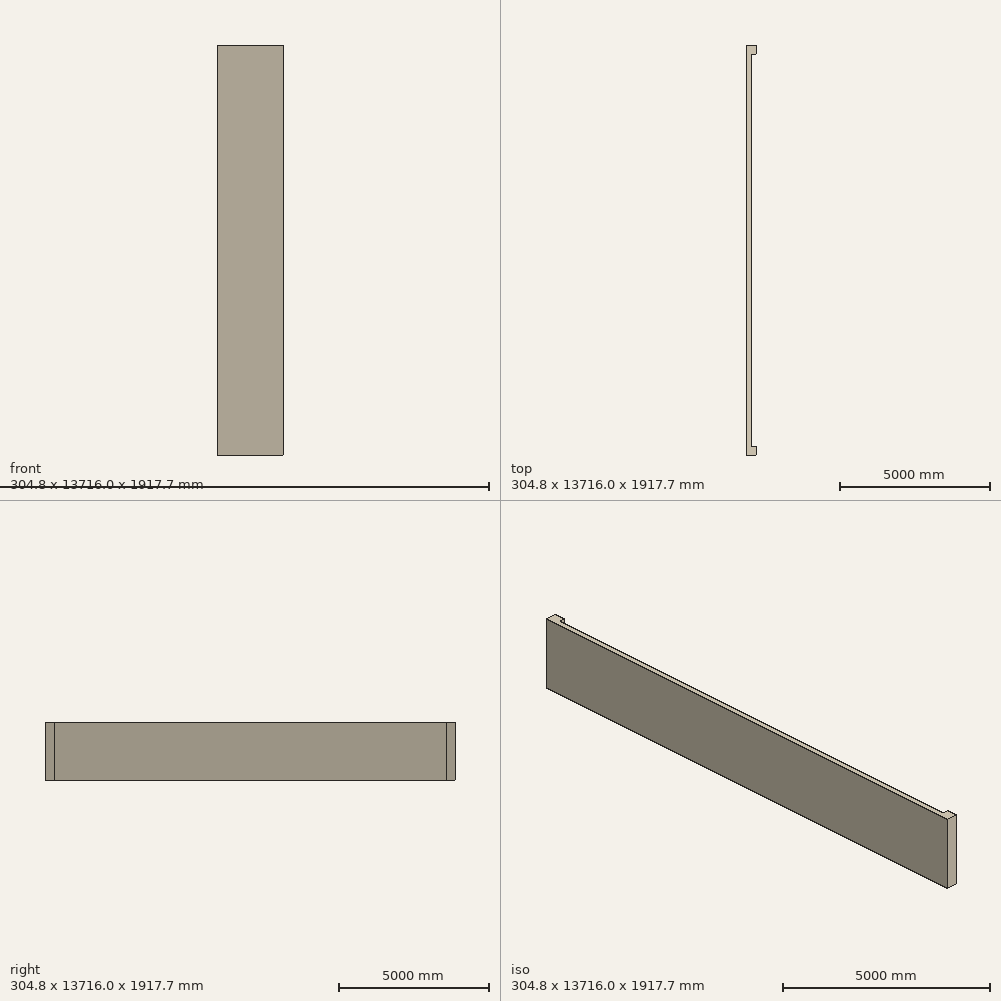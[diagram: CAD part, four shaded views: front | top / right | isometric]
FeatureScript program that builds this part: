
annotation { "Feature Type Name" : "Feature", "Feature Type Description" : "" }
export const myFeature = defineFeature(function(context is Context, id is Id, definition is map)
    precondition{}
    {
        {
            var Q0;
            Q0=qCreatedBy(makeId("Front.planeOp"),FACE);
            var sketch = newSketch(context, id + "F0", { "sketchPlane" : qUnion([Q0])});
            skLineSegment(sketch, "E0.bottom", {"start": v(0, 1917.7) * mm, "end": v(152.4, 1917.7) * mm});
            skLineSegment(sketch, "E0.top", {"start": v(0, 0) * mm, "end": v(152.4, 0) * mm});
            skLineSegment(sketch, "E0.left", {"start": v(0, 1917.7) * mm, "end": v(0, 0) * mm});
            skLineSegment(sketch, "E0.right", {"start": v(152.4, 1917.7) * mm, "end": v(152.4, 0) * mm});
            skSolve(sketch);
        }
        {
            var Q0;
            Q0 = qSketchRegion(id + "F0", true);
            extrude(context, id + "F1", {"entities" : qUnion([Q0]), "endBound" : BoundingType.SYMMETRIC, "depth" : 13716 * mm});
        }
        {
            var Q0;
            Q0=makeQuery(id+"F1.opExtrude","SWEPT_FACE",FACE,{"disambiguationData":[OSD([sQuery(id+"F0.wireOp",EDGE,"E0.right")])]});
            var sketch = newSketch(context, id + "F2", { "sketchPlane" : qUnion([Q0])});
            skLineSegment(sketch, "E1.bottom", {"start": v(-6858, 1917.7) * mm, "end": v(-6553.2, 1917.7) * mm});
            skLineSegment(sketch, "E1.top", {"start": v(-6858, 0) * mm, "end": v(-6553.2, 0) * mm});
            skLineSegment(sketch, "E1.left", {"start": v(-6858, 1917.7) * mm, "end": v(-6858, 0) * mm});
            skLineSegment(sketch, "E1.right", {"start": v(-6553.2, 1917.7) * mm, "end": v(-6553.2, 0) * mm});
            skLineSegment(sketch, "E2.bottom", {"start": v(6858, 1917.7) * mm, "end": v(6553.2, 1917.7) * mm});
            skLineSegment(sketch, "E2.top", {"start": v(6858, 0) * mm, "end": v(6553.2, 0) * mm});
            skLineSegment(sketch, "E2.left", {"start": v(6858, 1917.7) * mm, "end": v(6858, 0) * mm});
            skLineSegment(sketch, "E2.right", {"start": v(6553.2, 1917.7) * mm, "end": v(6553.2, 0) * mm});
            skSolve(sketch);
        }
        {
            var Q0;
            Q0 = qSketchRegion(id + "F2", true);
            extrude(context, id + "F3", {"entities" : qUnion([Q0]), "operationType" : NewBodyOperationType.ADD, "depth" : 152.4 * mm});
        }
    });
